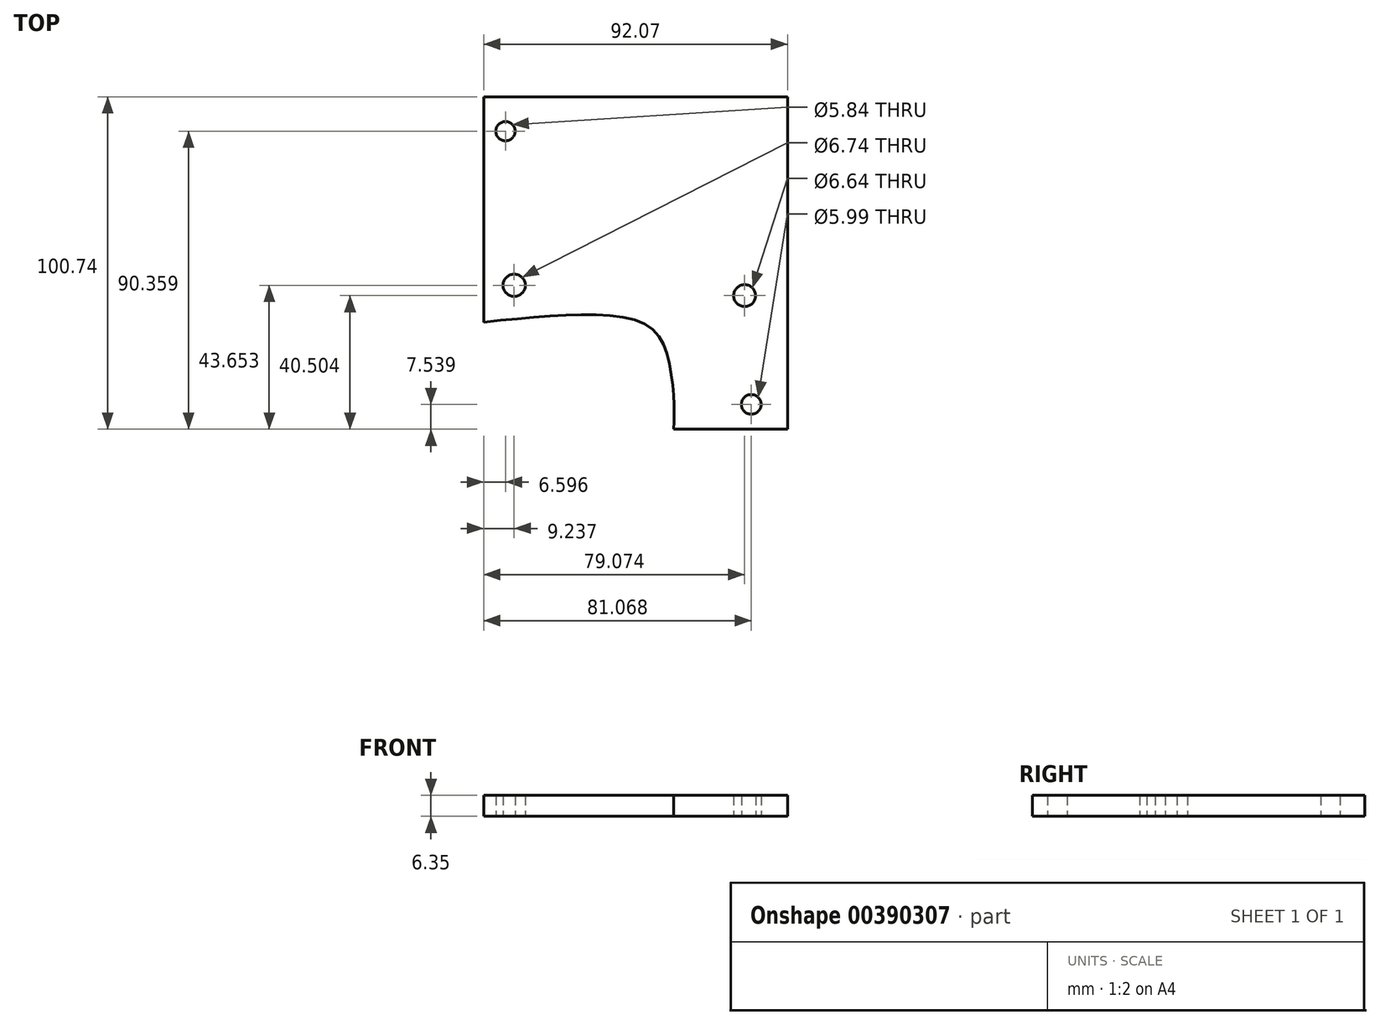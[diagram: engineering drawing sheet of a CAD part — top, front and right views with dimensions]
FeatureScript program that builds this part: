
annotation { "Feature Type Name" : "Feature", "Feature Type Description" : "" }
export const myFeature = defineFeature(function(context is Context, id is Id, definition is map)
    precondition{}
    {
        {
            var Q0;
            Q0=qCreatedBy(makeId("Top.planeOp"),FACE);
            var sketch = newSketch(context, id + "F0", { "sketchPlane" : qUnion([Q0])});
            skLineSegment(sketch, "E0", {"start": v(36.28, 44.85) * mm, "end": v(-55.8, 44.85) * mm});
            skLineSegment(sketch, "E1", {"start": v(-55.8, 44.85) * mm, "end": v(-55.8, -23.4) * mm});
            skLineSegment(sketch, "E2", {"start": v(36.28, 44.85) * mm, "end": v(36.28, -55.89) * mm});
            skLineSegment(sketch, "E3", {"start": v(1.8, -55.89) * mm, "end": v(36.28, -55.89) * mm});
            skFitSpline(sketch, "E4", {"points": [v(-55.8, -23.4) * mm, v(-23.58, -21.2) * mm, v(-5.52, -24.84) * mm, v(0, -34.2) * mm, v(1.86, -47.43) * mm, v(1.8, -55.89) * mm], "startDerivative": vector(117.18, 12.02) * mm, "endDerivative": vector(-2.11, -53.82) * mm});
            skCircle(sketch, "E5", {"center": v(-49.2, 34.47) * mm, "radius": 2.92 * mm});
            skCircle(sketch, "E6", {"center": v(-46.55, -12.24) * mm, "radius": 3.37 * mm});
            skCircle(sketch, "E7", {"center": v(23.28, -15.39) * mm, "radius": 3.32 * mm});
            skCircle(sketch, "E8", {"center": v(25.28, -48.35) * mm, "radius": 3 * mm});
            skSolve(sketch);
        }
        {
            var Q0;
            Q0=makeQuery(id+"F0.imprint","IMPRINT",FACE,{"disambiguationData":[TD([[makeQuery(id+"F0.imprint","IMPRINT",EDGE,{"derivedFrom":sQuery(id+"F0.wireOp",EDGE,"E0")}),1.0]])]});
            extrude(context, id + "F1", {"entities" : qUnion([Q0]), "depth" : 6.35 * mm});
        }
    });
